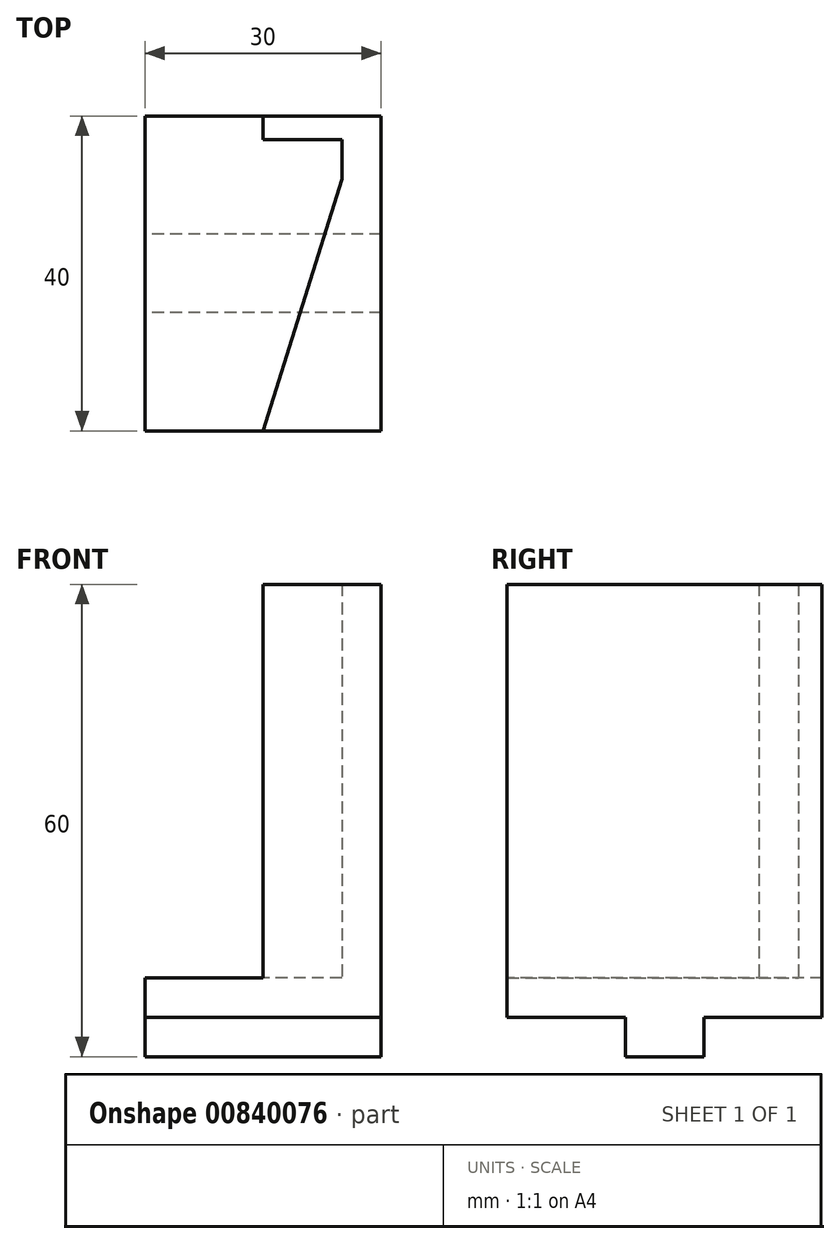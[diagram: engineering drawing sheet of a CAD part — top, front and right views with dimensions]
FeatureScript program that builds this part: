
annotation { "Feature Type Name" : "Feature", "Feature Type Description" : "" }
export const myFeature = defineFeature(function(context is Context, id is Id, definition is map)
    precondition{}
    {
        {
            var Q0;
            Q0=qCreatedBy(makeId("Top.planeOp"),FACE);
            var sketch = newSketch(context, id + "F0", { "sketchPlane" : qUnion([Q0])});
            skLineSegment(sketch, "E0.MirrorCS", {"start": v(0, 37) * mm, "end": v(0, 40) * mm});
            skLineSegment(sketch, "E1.MirrorCS", {"start": v(15, 0) * mm, "end": v(0, 0) * mm});
            skLineSegment(sketch, "E2.MirrorCS", {"start": v(10, 37) * mm, "end": v(0, 37) * mm});
            skLineSegment(sketch, "E3.MirrorCS", {"start": v(0, 40) * mm, "end": v(15, 40) * mm});
            skLineSegment(sketch, "E4.MirrorCS", {"start": v(10, 32) * mm, "end": v(10, 37) * mm});
            skLineSegment(sketch, "E5.MirrorCS", {"start": v(15, 40) * mm, "end": v(15, 0) * mm});
            skLineSegment(sketch, "E6.MirrorCS", {"start": v(0, 0) * mm, "end": v(10, 32) * mm});
            skSolve(sketch);
        }
        {
            var Q0;
            Q0 = qSketchRegion(id + "F0", true);
            extrude(context, id + "F1", {"entities" : qUnion([Q0]), "depth" : 50 * mm, "offsetDistance" : 25 * mm});
        }
        {
            var Q0;
            Q0=qCreatedBy(makeId("Right.planeOp"),FACE);
            var sketch = newSketch(context, id + "F2", { "sketchPlane" : qUnion([Q0])});
            skLineSegment(sketch, "E7", {"start": v(40, 0) * mm, "end": v(0, 0) * mm});
            skLineSegment(sketch, "E8", {"start": v(0, 0) * mm, "end": v(0, -5) * mm});
            skLineSegment(sketch, "E9", {"start": v(0, -5) * mm, "end": v(15, -5) * mm});
            skLineSegment(sketch, "E10", {"start": v(15, -5) * mm, "end": v(15, -10) * mm});
            skLineSegment(sketch, "E11", {"start": v(15, -10) * mm, "end": v(25, -10) * mm});
            skLineSegment(sketch, "E12", {"start": v(25, -10) * mm, "end": v(25, -5) * mm});
            skLineSegment(sketch, "E13", {"start": v(25, -5) * mm, "end": v(40, -5) * mm});
            skLineSegment(sketch, "E14", {"start": v(40, -5) * mm, "end": v(40, 0) * mm});
            skSolve(sketch);
        }
        {
            var Q0;
            Q0 = qSketchRegion(id + "F2", true);
            extrude(context, id + "F3", {"entities" : qUnion([Q0]), "operationType" : NewBodyOperationType.ADD, "depth" : 15 * mm, "offsetDistance" : 25 * mm});
        }
        {
            var Q0;
            Q0 = qSketchRegion(id + "F2", true);
            extrude(context, id + "F4", {"entities" : qUnion([Q0]), "operationType" : NewBodyOperationType.ADD, "oppositeDirection" : true, "depth" : 15 * mm, "offsetDistance" : 25 * mm});
        }
    });
